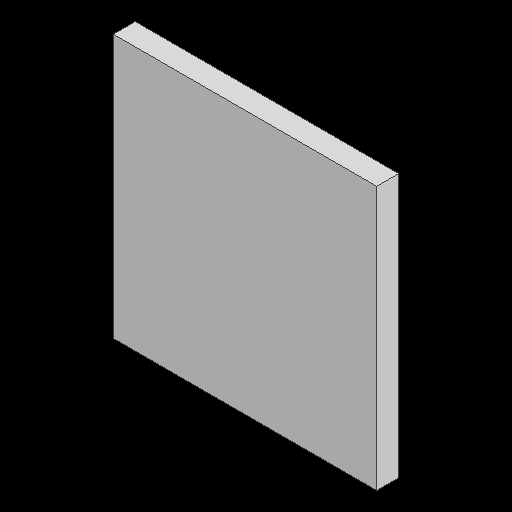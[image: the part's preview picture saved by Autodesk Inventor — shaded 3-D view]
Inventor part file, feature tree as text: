
AUTODESK INVENTOR PART (.ipt)
format: ipt  version: 2025.1 (Build 291241000, 241)  size: 78,336 bytes
history: native  units: in
note: dims shown in document units (in); Inventor stores cm internally (conversion verified against a paired STEP export)
features: other x1, extrude x1, sketch x1
ambient origin geometry x8: Origin, YZ Plane, XZ Plane, XY Plane, X Axis, Y Axis, Z Axis, Center Point
bodies: Body1 (feature_tree)
feature tree (3):
  other  "솔리드1"
  extrude  "돌출1"  Depth=0.7087in
  sketch  "스케치1"
